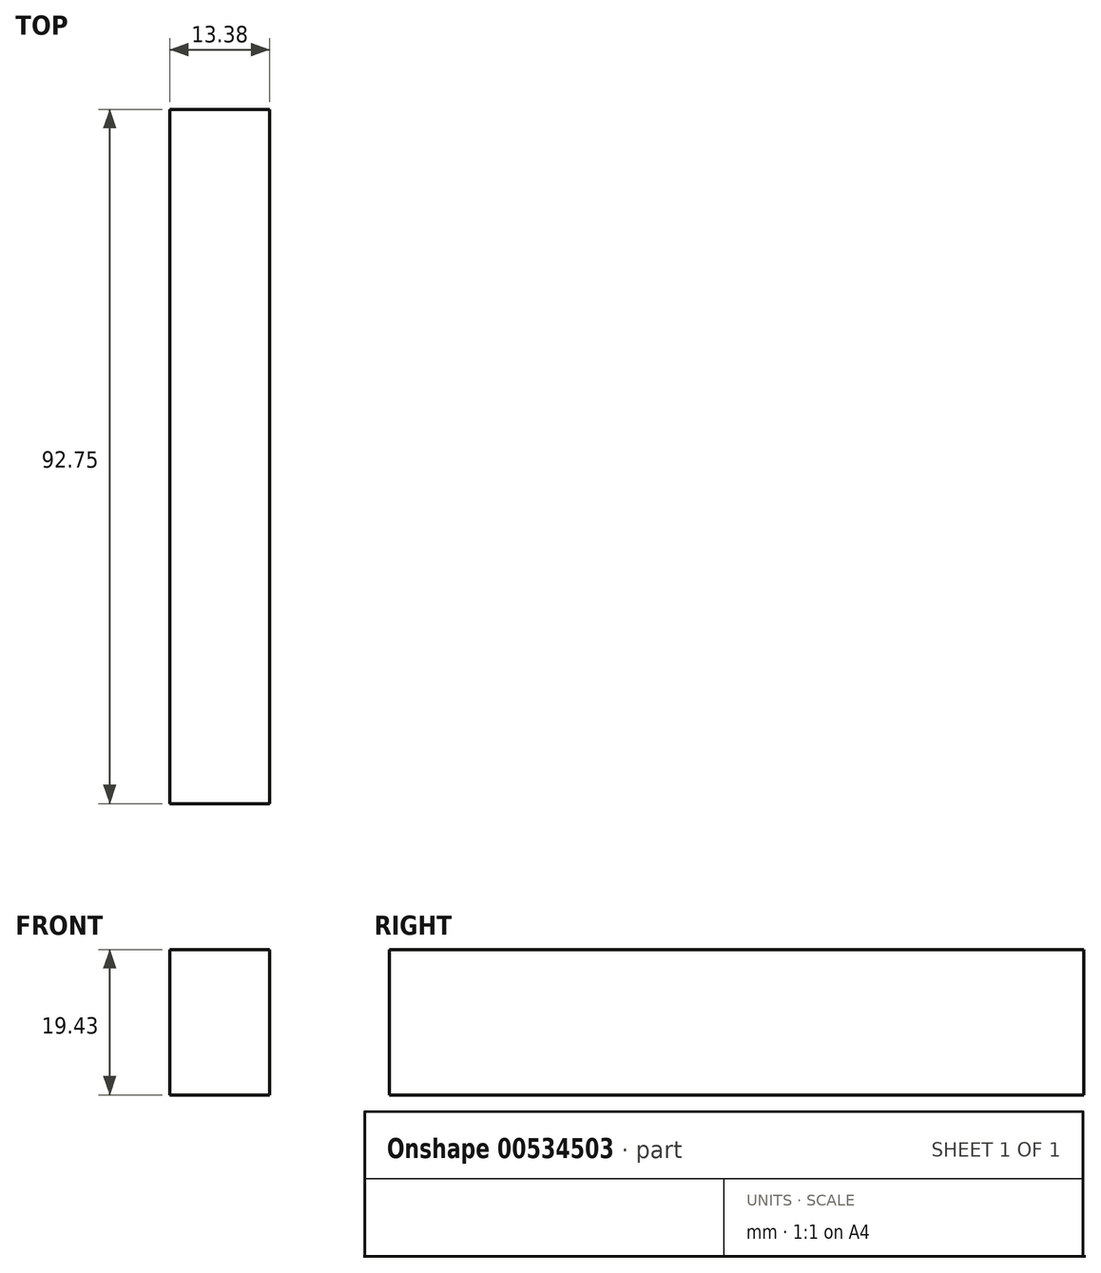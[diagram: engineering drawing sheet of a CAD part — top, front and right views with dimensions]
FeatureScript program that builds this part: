
annotation { "Feature Type Name" : "Feature", "Feature Type Description" : "" }
export const myFeature = defineFeature(function(context is Context, id is Id, definition is map)
    precondition{}
    {
        {
            var Q0;
            Q0=qCreatedBy(makeId("Right.planeOp"),FACE);
            var sketch = newSketch(context, id + "F0", { "sketchPlane" : qUnion([Q0])});
            skLineSegment(sketch, "E0.bottom", {"start": v(0, 19.43) * mm, "end": v(-92.75, 19.43) * mm});
            skLineSegment(sketch, "E0.top", {"start": v(0, 0) * mm, "end": v(-92.75, 0) * mm});
            skLineSegment(sketch, "E0.left", {"start": v(0, 19.43) * mm, "end": v(0, 0) * mm});
            skLineSegment(sketch, "E0.right", {"start": v(-92.75, 19.43) * mm, "end": v(-92.75, 0) * mm});
            skSolve(sketch);
        }
        {
            var Q0;
            Q0=makeQuery(id+"F0.imprint","IMPRINT",FACE,{"disambiguationData":[TD([[makeQuery(id+"F0.imprint","IMPRINT",EDGE,{"derivedFrom":sQuery(id+"F0.wireOp",EDGE,"E0.bottom")}),1.0]])]});
            var sketch = newSketch(context, id + "F1", { "sketchPlane" : qUnion([Q0])});
            skSolve(sketch);
        }
        {
            var Q0;
            Q0 = qSketchRegion(id + "F1", true);
            var Q1;
            Q1=makeQuery(id+"F0.imprint","IMPRINT",FACE,{"disambiguationData":[TD([[makeQuery(id+"F0.imprint","IMPRINT",EDGE,{"derivedFrom":sQuery(id+"F0.wireOp",EDGE,"E0.bottom")}),1.0]])]});
            extrude(context, id + "F2", {"entities" : qUnion([Q0, Q1]), "depth" : 13.38 * mm, "offsetDistance" : 25.4 * mm});
        }
    });
